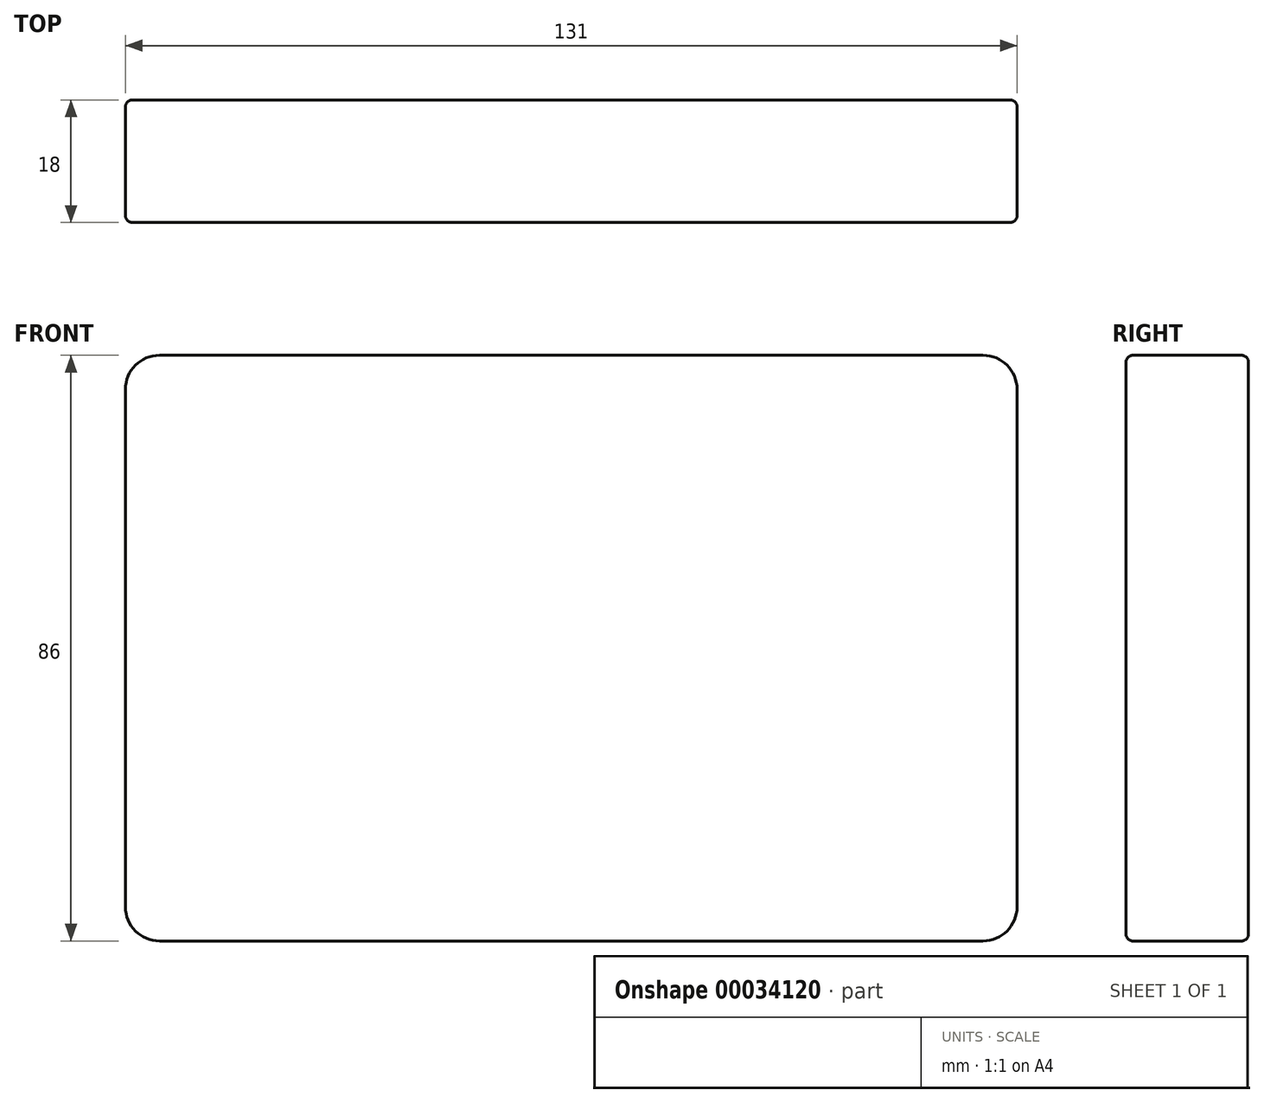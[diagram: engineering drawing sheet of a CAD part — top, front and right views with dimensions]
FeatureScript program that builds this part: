
annotation { "Feature Type Name" : "Feature", "Feature Type Description" : "" }
export const myFeature = defineFeature(function(context is Context, id is Id, definition is map)
    precondition{}
    {
        {
            var Q0;
            Q0=qCreatedBy(makeId("Front.planeOp"),FACE);
            var sketch = newSketch(context, id + "F0", { "sketchPlane" : qUnion([Q0])});
            skLineSegment(sketch, "E0.rect.bottom", {"start": v(65.5, -43) * mm, "end": v(-65.5, -43) * mm});
            skLineSegment(sketch, "E0.rect.top", {"start": v(65.5, 43) * mm, "end": v(-65.5, 43) * mm});
            skLineSegment(sketch, "E0.rect.left", {"start": v(65.5, -43) * mm, "end": v(65.5, 43) * mm});
            skLineSegment(sketch, "E0.rect.right", {"start": v(-65.5, -43) * mm, "end": v(-65.5, 43) * mm});
            skPoint(sketch, "E0.rect.middle", {"position": v(0, 0) * mm});
            skSolve(sketch);
        }
        {
            var Q0;
            Q0 = qSketchRegion(id + "F0", true);
            extrude(context, id + "F1", {"entities" : qUnion([Q0]), "oppositeDirection" : true, "depth" : 18 * mm});
        }
        {
            var Q0;
            Q0=makeQuery(id+"F1.opExtrude","SWEPT_EDGE",EDGE,{"disambiguationData":[OSD([sQuery(id+"F0.wireOp",EDGE,"E0.rect.top"),sQuery(id+"F0.wireOp",EDGE,"E0.rect.right")])]});
            var Q1;
            Q1=makeQuery(id+"F1.opExtrude","SWEPT_EDGE",EDGE,{"disambiguationData":[OSD([sQuery(id+"F0.wireOp",EDGE,"E0.rect.top"),sQuery(id+"F0.wireOp",EDGE,"E0.rect.left")])]});
            var Q2;
            Q2=makeQuery(id+"F1.opExtrude","SWEPT_EDGE",EDGE,{"disambiguationData":[OSD([sQuery(id+"F0.wireOp",EDGE,"E0.rect.bottom"),sQuery(id+"F0.wireOp",EDGE,"E0.rect.left")])]});
            var Q3;
            Q3=makeQuery(id+"F1.opExtrude","SWEPT_EDGE",EDGE,{"disambiguationData":[OSD([sQuery(id+"F0.wireOp",EDGE,"E0.rect.bottom"),sQuery(id+"F0.wireOp",EDGE,"E0.rect.right")])]});
            fillet(context, id + "F2", {"entities" : qUnion([Q0, Q1, Q2, Q3]), "radius" : 5 * mm, "tangentPropagation" : true, "allowEdgeOverflow" : false});
        }
        {
            var Q0;
            Q0=makeQuery(id+"F1.opExtrude","CAP_FACE",FACE,{"disambiguationData":[OSD([sQuery(id+"F0.wireOp",EDGE,"E0.rect.bottom"),sQuery(id+"F0.wireOp",EDGE,"E0.rect.top"),sQuery(id+"F0.wireOp",EDGE,"E0.rect.left"),sQuery(id+"F0.wireOp",EDGE,"E0.rect.right")])],"isStart":false});
            var Q1;
            Q1=makeQuery(id+"F1.opExtrude","CAP_FACE",FACE,{"disambiguationData":[OSD([sQuery(id+"F0.wireOp",EDGE,"E0.rect.bottom"),sQuery(id+"F0.wireOp",EDGE,"E0.rect.top"),sQuery(id+"F0.wireOp",EDGE,"E0.rect.left"),sQuery(id+"F0.wireOp",EDGE,"E0.rect.right")])],"isStart":true});
            fillet(context, id + "F3", {"entities" : qUnion([Q0, Q1]), "radius" : 1 * mm, "tangentPropagation" : true, "allowEdgeOverflow" : false});
        }
    });
